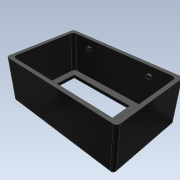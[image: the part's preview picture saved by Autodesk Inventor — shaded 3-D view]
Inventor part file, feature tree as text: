
AUTODESK INVENTOR PART (.ipt)
format: ipt  version: 2020.1 (Build 241239000, 239)  size: 265,728 bytes
history: native  units: in
note: dims shown in document units (in); Inventor stores cm internally (conversion verified against a paired STEP export)
features: reference x16, fillet x8, other x5, extrude x4, sketch x3, chamfer x2, shell x1, hole x1
ambient origin geometry x8: Origin, YZ Plane, XZ Plane, XY Plane, X Axis, Y Axis, Z Axis, Center Point
bodies: Solid1 (feature_tree)
feature tree (40):
  extrude  "Box-Extrude"  Depth=3.1496in
  shell  "Box-Shell"  Thickness=1.1811in
  extrude  "LCD-Extrude"  Depth=1.378in
  fillet  "Fillet1"  Radius=1.8701in
  fillet  "Fillet2"  Radius=3.0in
  fillet  "Fillet3"  Radius=0.0787in
  fillet  "Fillet4"  Radius=0.0787in
  fillet  "Fillet5"  Radius=0.0787in
  fillet  "Fillet6"  Radius=0.0787in
  fillet  "Fillet7"  Radius=0.0984in
  fillet  "Fillet8"  Radius=0.0984in
  extrude  "Extrusion10"  Depth=0.0984in
  chamfer  "Chamfer9"  Distance=0.1969in
  extrude  "Extrusion11"  Depth=0.9843in
  chamfer  "Chamfer10"  Distance=1.4764in
  hole  "Hole12"  [1 undecoded]
  other  "Box-Sketch"
  other  "LCD-Sketch"
  sketch  "Sketch16"  dims[d0=1.9685in d1=3.1496in d2=1.1811in d3=0.0in]
  reference  "Reference60"
  reference  "Reference61"
  reference  "Reference62"
  reference  "Reference63"
  reference  "Reference64"
  reference  "Reference65"
  reference  "Reference66"
  reference  "Reference67"
  sketch  "Sketch17"  dims[d4=0.0984in d41=1.378in d42=1.8701in d43=3.0in d44=0.0in d104=0.0787in d105=0.0787in d106=0.0787in d107=0.0787in d119=0.0984in d120=0.0984in]
  reference  "Reference68"
  reference  "Reference69"
  reference  "Reference70"
  reference  "Reference71"
  reference  "Reference72"
  reference  "Reference73"
  reference  "Reference74"
  reference  "Reference75"
  sketch  "Sketch20"  dims[d121=0.0984in d122=0.0984in d160=0.1969in d164=0.9843in d165=1.4764in d166=0.689in d167=0.689in d168=0.1969in d232=0.0984in d233=0.0984in d234=0.0984in d235=0.0984in d236=0.0984in d237=0.0in d238=0.0394in d239=0.0787in d240=45.0deg d241=0.0984in d242=0.0984in d243=0.0984in d244=0.0984in d245=0.0984in d246=0.0in d247=0.0394in d248=0.0787in d249=45.0deg d250=0.187in d251=0.187in d252=0.187in d253=0.187in d254=0.4528in d255=0.4528in d256=0.689in d257=0.689in d258=0.1969in d259=0.2362in d260=0.1575in d261=0.0787in d262=90.0deg d263=0.5906in d264=0.8108in]
  other  "<userpath>\Documents\Vault\Haynie Research\Telemetry\Receiver Box\Receiver Box.iam"
  other  "Receiver Box.iam"
  other  "receiver-box-lid:1"
note: 1 required parameter value undecoded (feature->parameter linkage not recoverable at this tier; creation-order binding heuristic only, values carry confidence <= 0.55)
